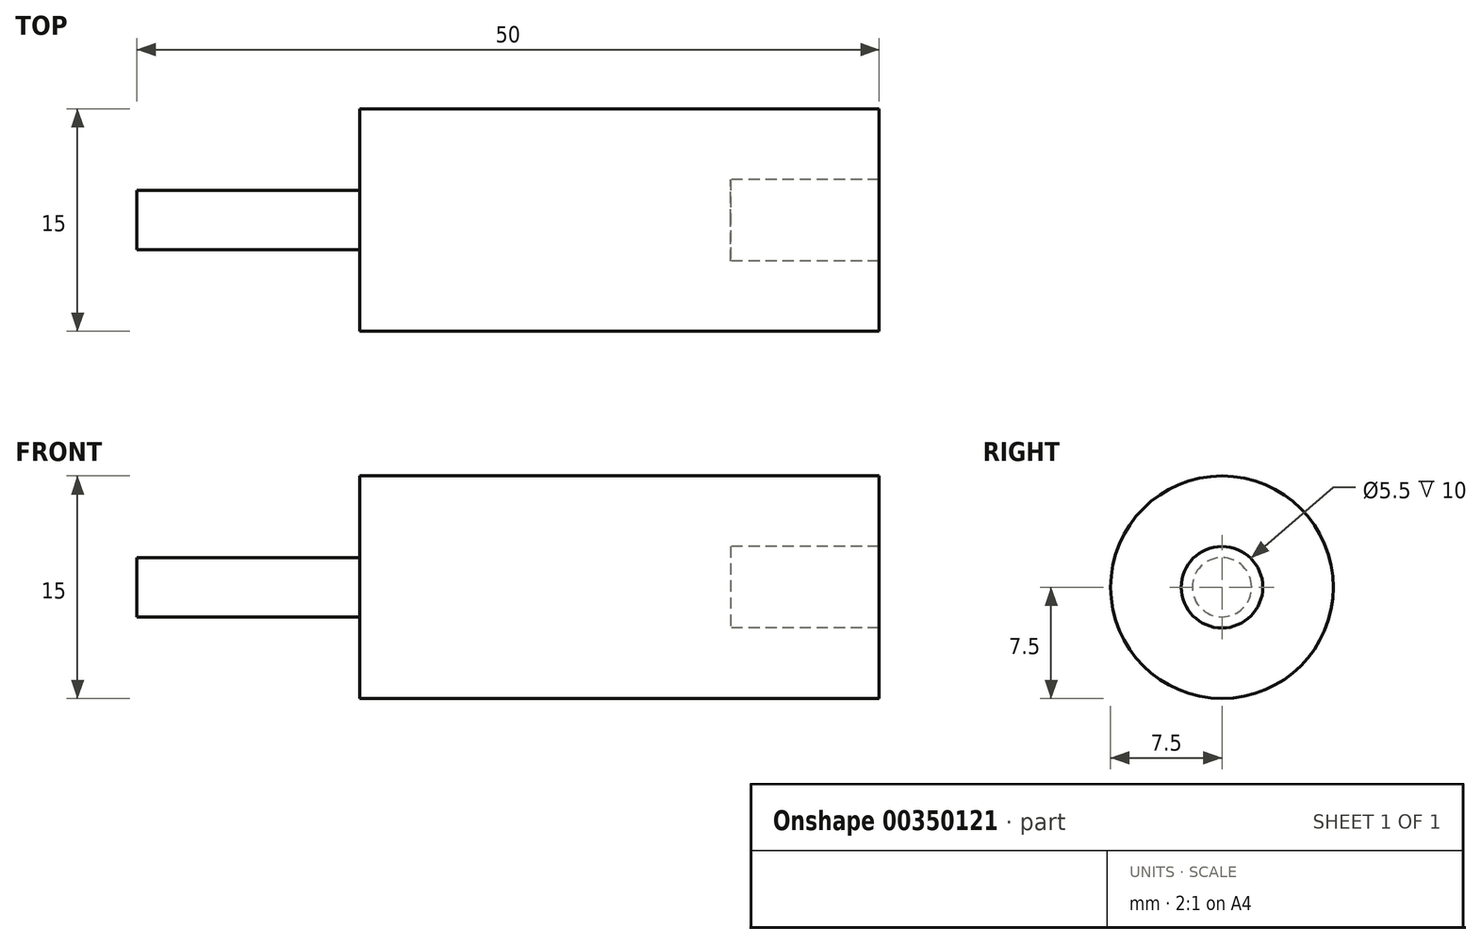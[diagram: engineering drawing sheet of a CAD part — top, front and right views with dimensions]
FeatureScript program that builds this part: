
annotation { "Feature Type Name" : "Feature", "Feature Type Description" : "" }
export const myFeature = defineFeature(function(context is Context, id is Id, definition is map)
    precondition{}
    {
        {
            var Q0;
            Q0=qCreatedBy(makeId("Front.planeOp"),FACE);
            var sketch = newSketch(context, id + "F0", { "sketchPlane" : qUnion([Q0])});
            skLineSegment(sketch, "E0.top", {"start": v(10, -4.75) * mm, "end": v(-25, -4.75) * mm});
            skPoint(sketch, "E0.middle", {"position": v(0, 0) * mm});
            skPoint(sketch, "E1.middle", {"position": v(-50, 0) * mm});
            skLineSegment(sketch, "E2.right", {"start": v(-40, 2.75) * mm, "end": v(-40, 0.75) * mm});
            skLineSegment(sketch, "E3", {"start": v(-25, 2.75) * mm, "end": v(-25, -4.75) * mm});
            skLineSegment(sketch, "E4", {"start": v(0, 2.75) * mm, "end": v(0, 0) * mm});
            skLineSegment(sketch, "E5", {"start": v(-40, 2.75) * mm, "end": v(-25, 2.75) * mm});
            skLineSegment(sketch, "E6", {"start": v(-25, 2.75) * mm, "end": v(0, 2.75) * mm});
            skLineSegment(sketch, "E7", {"start": v(10, 0) * mm, "end": v(10, -4.75) * mm});
            skLineSegment(sketch, "E8", {"start": v(-40, 0.75) * mm, "end": v(-25, 0.75) * mm});
            skLineSegment(sketch, "E9", {"start": v(-40, 2.75) * mm, "end": v(0, 2.75) * mm});
            skLineSegment(sketch, "E10", {"start": v(10, 0) * mm, "end": v(0, 0) * mm});
            skSolve(sketch);
        }
        {
            var Q0;
            Q0 = qSketchRegion(id + "F0", true);
            var Q1;
            Q1=sQuery(id+"F0.wireOp",EDGE,"E9");
            revolve(context, id + "F1", {"entities" : qUnion([Q0]), "axis" : qUnion([Q1]), "revolveType" : RevolveType.FULL});
        }
    });
